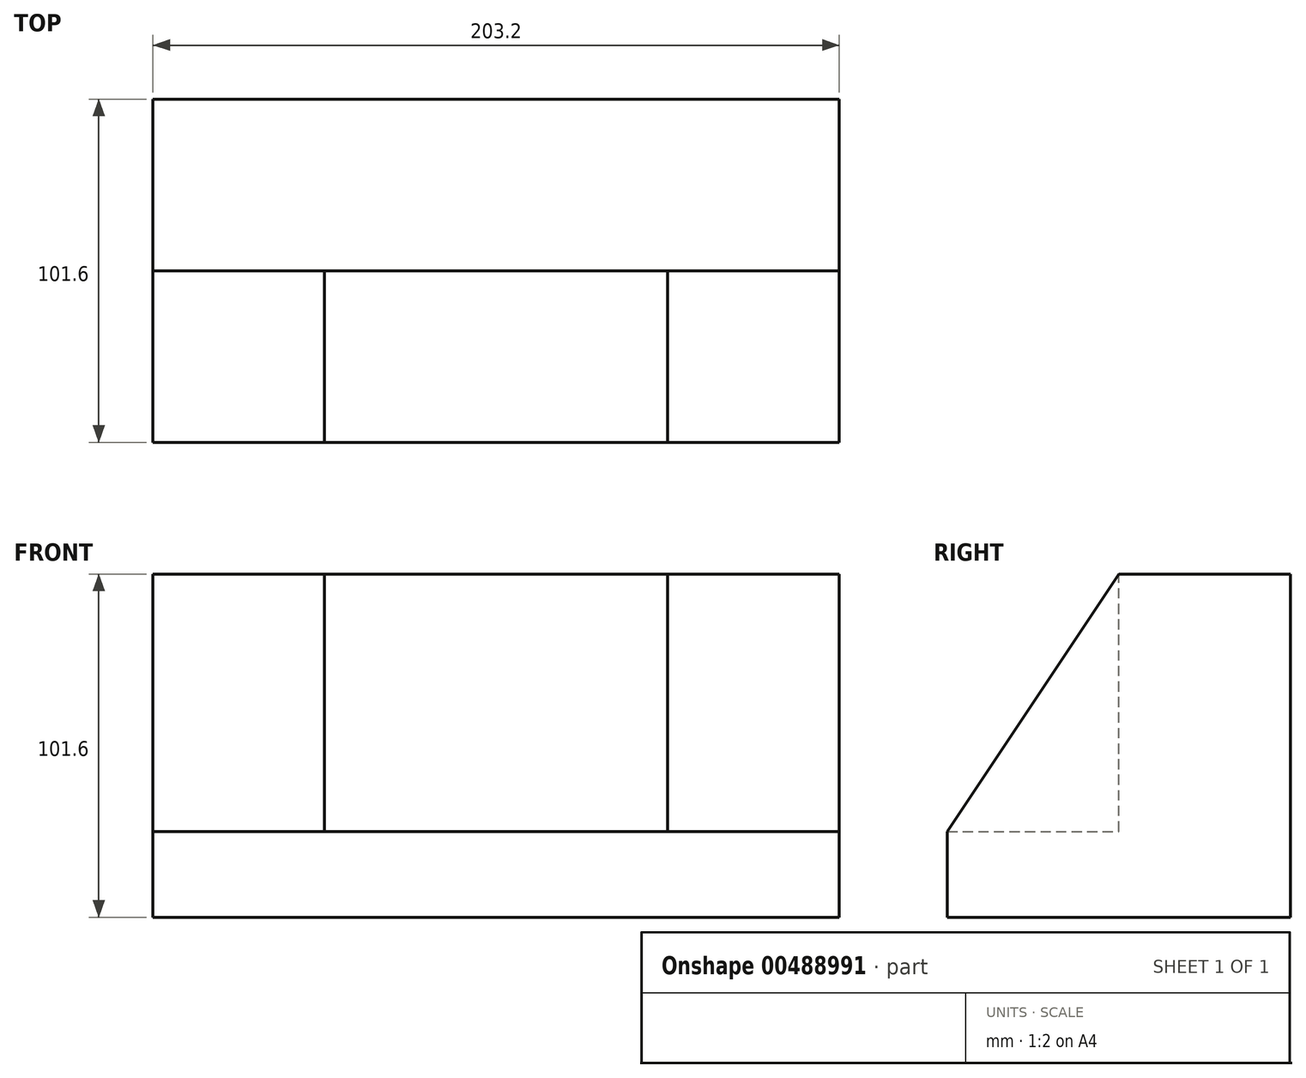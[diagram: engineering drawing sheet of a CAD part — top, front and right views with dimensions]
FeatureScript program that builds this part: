
annotation { "Feature Type Name" : "Feature", "Feature Type Description" : "" }
export const myFeature = defineFeature(function(context is Context, id is Id, definition is map)
    precondition{}
    {
        {
            var Q0;
            Q0=qCreatedBy(makeId("Top.planeOp"),FACE);
            var sketch = newSketch(context, id + "F0", { "sketchPlane" : qUnion([Q0])});
            skLineSegment(sketch, "E0.bottom", {"start": v(-108.22, 55.17) * mm, "end": v(94.98, 55.17) * mm});
            skLineSegment(sketch, "E0.top", {"start": v(-108.22, -46.43) * mm, "end": v(94.98, -46.43) * mm});
            skLineSegment(sketch, "E0.left", {"start": v(-108.22, 55.17) * mm, "end": v(-108.22, -46.43) * mm});
            skLineSegment(sketch, "E0.right", {"start": v(94.98, 55.17) * mm, "end": v(94.98, -46.43) * mm});
            skSolve(sketch);
        }
        {
            var Q0;
            Q0 = qSketchRegion(id + "F0", true);
            extrude(context, id + "F1", {"entities" : qUnion([Q0]), "depth" : 101.6 * mm});
        }
        {
            var Q0;
            Q0=makeQuery(id+"F1.opExtrude","CAP_FACE",FACE,{"disambiguationData":[OSD([sQuery(id+"F0.wireOp",EDGE,"E0.bottom"),sQuery(id+"F0.wireOp",EDGE,"E0.top"),sQuery(id+"F0.wireOp",EDGE,"E0.left"),sQuery(id+"F0.wireOp",EDGE,"E0.right")])],"isStart":false});
            var sketch = newSketch(context, id + "F2", { "sketchPlane" : qUnion([Q0])});
            skLineSegment(sketch, "E1.bottom", {"start": v(-57.42, -46.43) * mm, "end": v(44.18, -46.43) * mm});
            skLineSegment(sketch, "E1.top", {"start": v(-57.42, 4.37) * mm, "end": v(44.18, 4.37) * mm});
            skLineSegment(sketch, "E1.left", {"start": v(-57.42, -46.43) * mm, "end": v(-57.42, 4.37) * mm});
            skLineSegment(sketch, "E1.right", {"start": v(44.18, -46.43) * mm, "end": v(44.18, 4.37) * mm});
            skSolve(sketch);
        }
        {
            var Q0;
            Q0 = qSketchRegion(id + "F2", true);
            extrude(context, id + "F3", {"entities" : qUnion([Q0]), "operationType" : NewBodyOperationType.REMOVE, "oppositeDirection" : true, "depth" : 76.2 * mm});
        }
        {
            var Q0;
            Q0=makeQuery(id+"F1.opExtrude","SWEPT_FACE",FACE,{"disambiguationData":[OSD([sQuery(id+"F0.wireOp",EDGE,"E0.right")])]});
            var sketch = newSketch(context, id + "F4", { "sketchPlane" : qUnion([Q0])});
            skLineSegment(sketch, "E2", {"start": v(4.37, 101.6) * mm, "end": v(-46.43, 25.4) * mm});
            skSolve(sketch);
        }
        {
            var Q0;
            {var subQ0=sQuery(id+"F4.wireOp",EDGE,"E2");Q0=makeQuery(id+"F4.imprint","IMPRINT",FACE,{"disambiguationData":[TD([[makeQuery(id+"F4.imprint","IMPRINT",EDGE,{"derivedFrom":subQ0}),-1.0]])]});}
            var Q1;
            Q1 = qSketchRegion(id + "F4", true);
            extrude(context, id + "F5", {"entities" : qUnion([Q0, Q1]), "operationType" : NewBodyOperationType.REMOVE, "endBound" : BoundingType.THROUGH_ALL, "oppositeDirection" : true, "depth" : 25.4 * mm});
        }
    });
